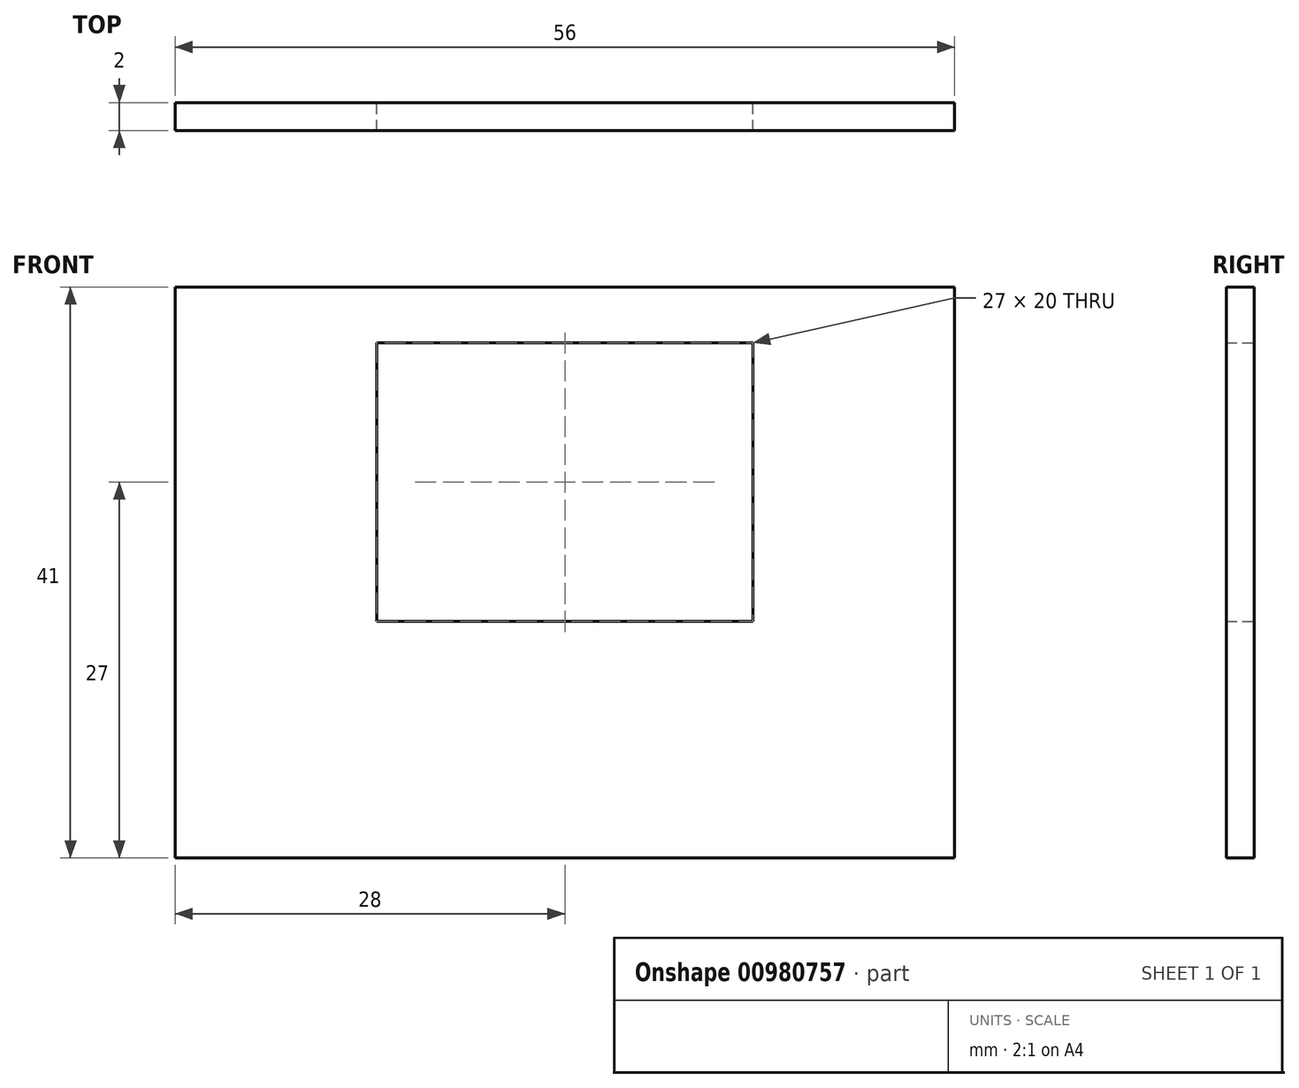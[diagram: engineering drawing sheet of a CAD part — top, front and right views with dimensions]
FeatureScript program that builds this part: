
annotation { "Feature Type Name" : "Feature", "Feature Type Description" : "" }
export const myFeature = defineFeature(function(context is Context, id is Id, definition is map)
    precondition{}
    {
        {
            var Q0;
            Q0=qCreatedBy(makeId("Front.planeOp"),FACE);
            var sketch = newSketch(context, id + "F0", { "sketchPlane" : qUnion([Q0])});
            skLineSegment(sketch, "E0.bottom", {"start": v(28, 20.5) * mm, "end": v(-28, 20.5) * mm});
            skLineSegment(sketch, "E0.top", {"start": v(28, -20.5) * mm, "end": v(-28, -20.5) * mm});
            skLineSegment(sketch, "E0.left", {"start": v(28, 20.5) * mm, "end": v(28, 16.5) * mm});
            skLineSegment(sketch, "E0.right", {"start": v(-28, 20.5) * mm, "end": v(-28, 16.5) * mm});
            skPoint(sketch, "E0.middle", {"position": v(0, 0) * mm});
            skLineSegment(sketch, "E1", {"start": v(-28, -3.5) * mm, "end": v(28, -3.5) * mm, "construction": true});
            skLineSegment(sketch, "E2", {"start": v(-28, 16.5) * mm, "end": v(28, 16.5) * mm, "construction": true});
            skLineSegment(sketch, "E3", {"start": v(-28, 16.5) * mm, "end": v(-28, -3.5) * mm});
            skLineSegment(sketch, "E4", {"start": v(-28, -3.5) * mm, "end": v(-28, -20.5) * mm});
            skLineSegment(sketch, "E5", {"start": v(28, -3.5) * mm, "end": v(28, -20.5) * mm});
            skLineSegment(sketch, "E6", {"start": v(28, 16.5) * mm, "end": v(28, -3.5) * mm});
            skLineSegment(sketch, "E7", {"start": v(0, 20.5) * mm, "end": v(0, -3.5) * mm, "construction": true});
            skLineSegment(sketch, "E8.bottom", {"start": v(13.5, 16.5) * mm, "end": v(-13.5, 16.5) * mm});
            skLineSegment(sketch, "E8.top", {"start": v(13.5, -3.5) * mm, "end": v(-13.5, -3.5) * mm});
            skLineSegment(sketch, "E8.left", {"start": v(13.5, 16.5) * mm, "end": v(13.5, 1) * mm});
            skLineSegment(sketch, "E8.right", {"start": v(-13.5, 16.5) * mm, "end": v(-13.5, 1) * mm});
            skPoint(sketch, "E8.middle", {"position": v(0, 6.5) * mm});
            skLineSegment(sketch, "E9", {"start": v(-13.5, 1) * mm, "end": v(-13.5, 1) * mm});
            skLineSegment(sketch, "E10", {"start": v(-13.5, 1) * mm, "end": v(13.5, 1) * mm, "construction": true});
            skLineSegment(sketch, "E11", {"start": v(-13.5, 1) * mm, "end": v(-13.5, -3.5) * mm});
            skLineSegment(sketch, "E12", {"start": v(13.5, 1) * mm, "end": v(13.5, -3.5) * mm});
            skLineSegment(sketch, "E13", {"start": v(-13.5, 8.75) * mm, "end": v(13.5, 8.75) * mm, "construction": true});
            skLineSegment(sketch, "E14.bottom", {"start": v(10.87, 3.32) * mm, "end": v(-10.87, 3.32) * mm});
            skLineSegment(sketch, "E14.top", {"start": v(10.87, 14.18) * mm, "end": v(-10.87, 14.18) * mm});
            skLineSegment(sketch, "E14.left", {"start": v(10.87, 3.32) * mm, "end": v(10.87, 14.18) * mm});
            skLineSegment(sketch, "E14.right", {"start": v(-10.87, 3.32) * mm, "end": v(-10.87, 14.18) * mm});
            skPoint(sketch, "E14.middle", {"position": v(0, 8.75) * mm});
            skSolve(sketch);
        }
        {
            var Q0;
            Q0 = qSketchRegion(id + "F0", true);
            extrude(context, id + "F1", {"entities" : qUnion([Q0]), "depth" : 2 * mm, "offsetDistance" : 25 * mm});
        }
    });
